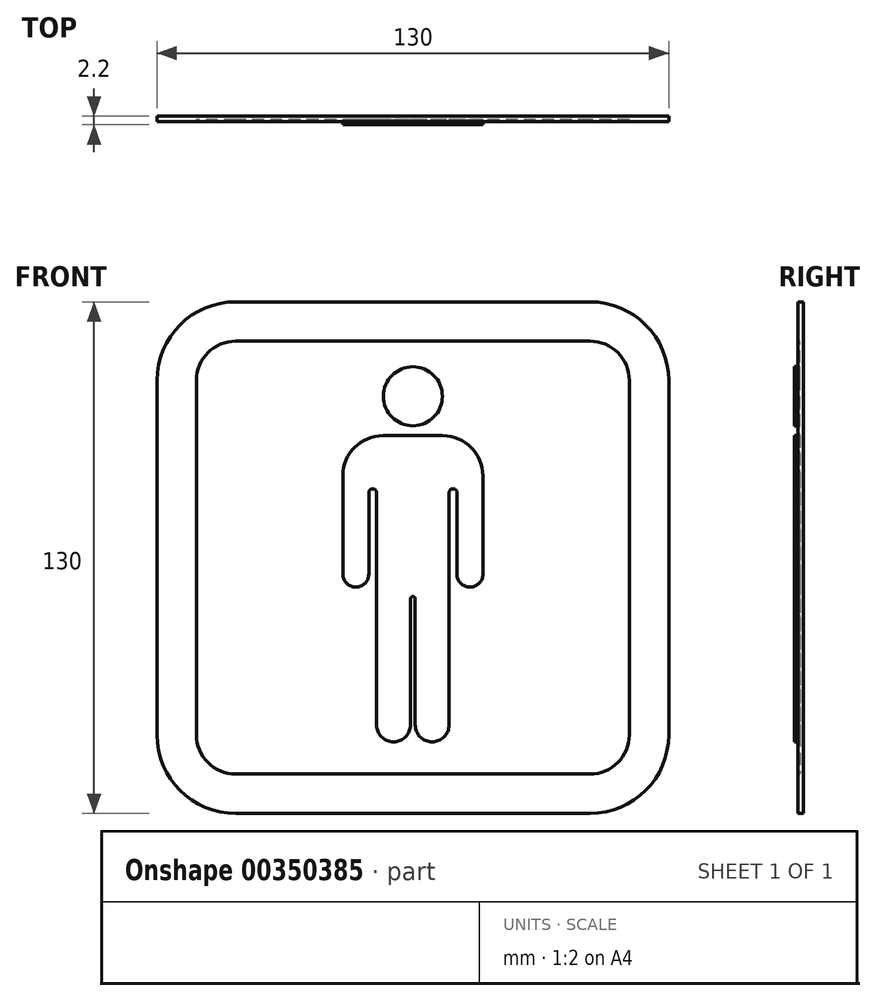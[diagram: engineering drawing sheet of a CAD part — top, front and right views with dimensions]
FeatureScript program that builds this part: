
annotation { "Feature Type Name" : "Feature", "Feature Type Description" : "" }
export const myFeature = defineFeature(function(context is Context, id is Id, definition is map)
    precondition{}
    {
        {
            var Q0;
            Q0=qCreatedBy(makeId("Front.planeOp"),FACE);
            var sketch = newSketch(context, id + "F0", { "sketchPlane" : qUnion([Q0])});
            skLineSegment(sketch, "E0.bottom", {"start": v(20, 0) * mm, "end": v(65, 0) * mm});
            skLineSegment(sketch, "E0.top", {"start": v(20, 130) * mm, "end": v(65, 130) * mm});
            skLineSegment(sketch, "E0.left", {"start": v(0, 20) * mm, "end": v(0, 110) * mm});
            skArc(sketch, "E1", {"start": v(65, 113.5) * mm, "mid": v(57.5, 106) * mm, "end": v(65, 98.5) * mm});
            skArc(sketch, "E2", {"start": v(57.42, 96) * mm, "mid": v(50.2, 93.01) * mm, "end": v(47.21, 85.8) * mm});
            skArc(sketch, "E3", {"start": v(47.21, 60.8) * mm, "mid": v(50.5, 57.5) * mm, "end": v(53.8, 60.8) * mm});
            skArc(sketch, "E4", {"start": v(55.8, 81.5) * mm, "mid": v(54.8, 82.5) * mm, "end": v(53.8, 81.5) * mm});
            skArc(sketch, "E5", {"start": v(55.8, 22.5) * mm, "mid": v(60.1, 18.2) * mm, "end": v(64.4, 22.5) * mm});
            skLineSegment(sketch, "E6", {"start": v(57.42, 96) * mm, "end": v(65, 96) * mm});
            skLineSegment(sketch, "E7", {"start": v(47.21, 85.8) * mm, "end": v(47.21, 60.8) * mm});
            skLineSegment(sketch, "E8", {"start": v(53.8, 81.5) * mm, "end": v(53.8, 60.8) * mm});
            skLineSegment(sketch, "E9", {"start": v(55.8, 81.5) * mm, "end": v(55.8, 22.5) * mm});
            skLineSegment(sketch, "E10", {"start": v(64.4, 54.5) * mm, "end": v(64.4, 22.5) * mm});
            skArc(sketch, "E11", {"start": v(0, 20) * mm, "mid": v(5.86, 5.86) * mm, "end": v(20, 0) * mm});
            skArc(sketch, "E12", {"start": v(20, 130) * mm, "mid": v(5.86, 124.14) * mm, "end": v(0, 110) * mm});
            skPoint(sketch, "E13.orphan", {"position": v(0, 130) * mm});
            skPoint(sketch, "E14.orphan", {"position": v(0, 0) * mm});
            skArc(sketch, "E15.MirrorCS", {"start": v(110, 130) * mm, "mid": v(124.14, 124.14) * mm, "end": v(130, 110) * mm});
            skLineSegment(sketch, "E16.MirrorCS", {"start": v(110, 130) * mm, "end": v(65, 130) * mm});
            skLineSegment(sketch, "E17.MirrorCS", {"start": v(130, 20) * mm, "end": v(130, 110) * mm});
            skArc(sketch, "E18.MirrorCS", {"start": v(130, 20) * mm, "mid": v(124.14, 5.86) * mm, "end": v(110, 0) * mm});
            skLineSegment(sketch, "E19.MirrorCS", {"start": v(110, 0) * mm, "end": v(65, 0) * mm});
            skLineSegment(sketch, "E20.0", {"start": v(110, 120) * mm, "end": v(65, 120) * mm});
            skLineSegment(sketch, "E20.1", {"start": v(20, 120) * mm, "end": v(65, 120) * mm});
            skArc(sketch, "E20.2", {"start": v(110, 120) * mm, "mid": v(117.07, 117.07) * mm, "end": v(120, 110) * mm});
            skArc(sketch, "E20.3", {"start": v(20, 120) * mm, "mid": v(12.93, 117.07) * mm, "end": v(10, 110) * mm});
            skLineSegment(sketch, "E20.4", {"start": v(10, 20) * mm, "end": v(10, 110) * mm});
            skArc(sketch, "E20.5", {"start": v(10, 20) * mm, "mid": v(12.93, 12.93) * mm, "end": v(20, 10) * mm});
            skLineSegment(sketch, "E20.6", {"start": v(120, 20) * mm, "end": v(120, 110) * mm});
            skArc(sketch, "E20.7", {"start": v(120, 20) * mm, "mid": v(117.07, 12.93) * mm, "end": v(110, 10) * mm});
            skLineSegment(sketch, "E20.8", {"start": v(110, 10) * mm, "end": v(65, 10) * mm});
            skLineSegment(sketch, "E20.9", {"start": v(20, 10) * mm, "end": v(65, 10) * mm});
            skArc(sketch, "E21", {"start": v(65, 55.1) * mm, "mid": v(64.58, 54.92) * mm, "end": v(64.4, 54.5) * mm});
            skArc(sketch, "E22.MirrorCS", {"start": v(65, 113.5) * mm, "mid": v(72.5, 106) * mm, "end": v(65, 98.5) * mm});
            skLineSegment(sketch, "E23.MirrorCS", {"start": v(72.58, 96) * mm, "end": v(65, 96) * mm});
            skArc(sketch, "E24.MirrorCS", {"start": v(72.58, 96) * mm, "mid": v(79.8, 93.01) * mm, "end": v(82.79, 85.8) * mm});
            skArc(sketch, "E25.MirrorCS", {"start": v(74.2, 81.5) * mm, "mid": v(75.2, 82.5) * mm, "end": v(76.2, 81.5) * mm});
            skLineSegment(sketch, "E26.MirrorCS", {"start": v(74.2, 81.5) * mm, "end": v(74.2, 22.5) * mm});
            skLineSegment(sketch, "E27.MirrorCS", {"start": v(76.2, 81.5) * mm, "end": v(76.2, 60.8) * mm});
            skLineSegment(sketch, "E28.MirrorCS", {"start": v(82.79, 85.8) * mm, "end": v(82.79, 60.8) * mm});
            skArc(sketch, "E29.MirrorCS", {"start": v(82.79, 60.8) * mm, "mid": v(79.5, 57.5) * mm, "end": v(76.2, 60.8) * mm});
            skArc(sketch, "E30.MirrorCS", {"start": v(74.2, 22.5) * mm, "mid": v(69.9, 18.2) * mm, "end": v(65.6, 22.5) * mm});
            skLineSegment(sketch, "E31.MirrorCS", {"start": v(65.6, 54.5) * mm, "end": v(65.6, 22.5) * mm});
            skArc(sketch, "E32.MirrorCS", {"start": v(65, 55.1) * mm, "mid": v(65.42, 54.92) * mm, "end": v(65.6, 54.5) * mm});
            skSolve(sketch);
        }
        {
            var Q0;
            Q0=makeQuery(id+"F0.imprint","IMPRINT",FACE,{"disambiguationData":[TD([[makeQuery(id+"F0.imprint","IMPRINT",EDGE,{"derivedFrom":sQuery(id+"F0.wireOp",EDGE,"E0.bottom")}),1.0]])]});
            var Q1;
            Q1=makeQuery(id+"F0.imprint","IMPRINT",FACE,{"disambiguationData":[TD([[makeQuery(id+"F0.imprint","IMPRINT",EDGE,{"derivedFrom":sQuery(id+"F0.wireOp",EDGE,"E1")}),-1.0]])]});
            var Q2;
            Q2=makeQuery(id+"F0.imprint","IMPRINT",FACE,{"disambiguationData":[TD([[makeQuery(id+"F0.imprint","IMPRINT",EDGE,{"derivedFrom":sQuery(id+"F0.wireOp",EDGE,"E2")}),1.0]])]});
            var Q3;
            Q3=makeQuery(id+"F0.imprint","IMPRINT",FACE,{"disambiguationData":[TD([[makeQuery(id+"F0.imprint","IMPRINT",EDGE,{"derivedFrom":sQuery(id+"F0.wireOp",EDGE,"E1")}),1.0]])]});
            extrude(context, id + "F1", {"entities" : qUnion([Q0, Q1, Q2, Q3]), "oppositeDirection" : true, "depth" : 0.9 * mm});
        }
        {
            var Q0;
            Q0=makeQuery(id+"F0.imprint","IMPRINT",FACE,{"disambiguationData":[TD([[makeQuery(id+"F0.imprint","IMPRINT",EDGE,{"derivedFrom":sQuery(id+"F0.wireOp",EDGE,"E0.bottom")}),1.0]])]});
            extrude(context, id + "F2", {"entities" : qUnion([Q0]), "operationType" : NewBodyOperationType.ADD, "depth" : 0.5 * mm});
        }
        {
            var Q0;
            Q0=makeQuery(id+"F0.imprint","IMPRINT",FACE,{"disambiguationData":[TD([[makeQuery(id+"F0.imprint","IMPRINT",EDGE,{"derivedFrom":sQuery(id+"F0.wireOp",EDGE,"E1")}),1.0]])]});
            var Q1;
            Q1=makeQuery(id+"F0.imprint","IMPRINT",FACE,{"disambiguationData":[TD([[makeQuery(id+"F0.imprint","IMPRINT",EDGE,{"derivedFrom":sQuery(id+"F0.wireOp",EDGE,"E2")}),1.0]])]});
            extrude(context, id + "F3", {"entities" : qUnion([Q0, Q1]), "operationType" : NewBodyOperationType.ADD, "depth" : 1.3 * mm});
        }
    });
